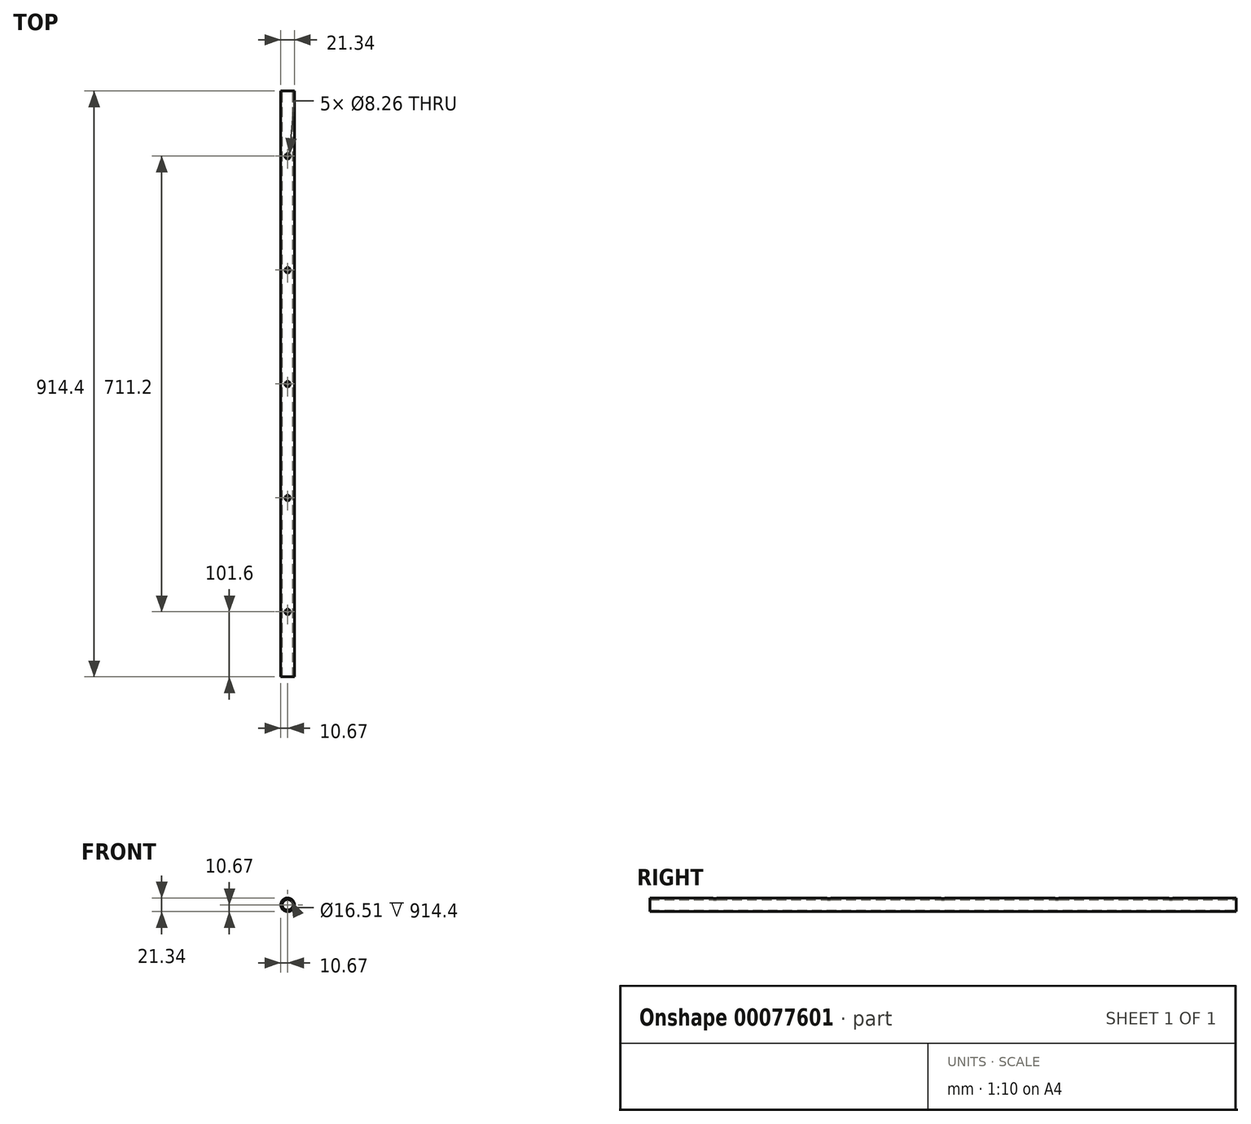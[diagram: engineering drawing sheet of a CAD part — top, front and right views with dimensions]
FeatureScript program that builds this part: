
annotation { "Feature Type Name" : "Feature", "Feature Type Description" : "" }
export const myFeature = defineFeature(function(context is Context, id is Id, definition is map)
    precondition{}
    {
        {
            var Q0;
            Q0=qCreatedBy(makeId("Front.planeOp"),FACE);
            var sketch = newSketch(context, id + "F0", { "sketchPlane" : qUnion([Q0])});
            skCircle(sketch, "E0", {"center": v(0, 0) * mm, "radius": 8.25 * mm});
            skCircle(sketch, "E1", {"center": v(0, 0) * mm, "radius": 10.67 * mm});
            skSolve(sketch);
        }
        {
            var Q0;
            Q0 = qSketchRegion(id + "F0", true);
            extrude(context, id + "F1", {"entities" : qUnion([Q0]), "depth" : 914.4 * mm});
        }
        {
            var Q0;
            Q0=qCreatedBy(makeId("Top.planeOp"),FACE);
            var sketch = newSketch(context, id + "F2", { "sketchPlane" : qUnion([Q0])});
            skCircle(sketch, "E2", {"center": v(0, -101.6) * mm, "radius": 4.13 * mm});
            skCircle(sketch, "E3", {"center": v(0, -279.4) * mm, "radius": 4.13 * mm});
            skCircle(sketch, "E4", {"center": v(0, -457.2) * mm, "radius": 4.13 * mm});
            skCircle(sketch, "E5", {"center": v(0, -635) * mm, "radius": 4.13 * mm});
            skCircle(sketch, "E6", {"center": v(0, -812.8) * mm, "radius": 4.13 * mm});
            skSolve(sketch);
        }
        {
            var Q0;
            Q0 = qSketchRegion(id + "F2", true);
            extrude(context, id + "F3", {"entities" : qUnion([Q0]), "operationType" : NewBodyOperationType.REMOVE, "depth" : 25.4 * mm});
        }
    });
